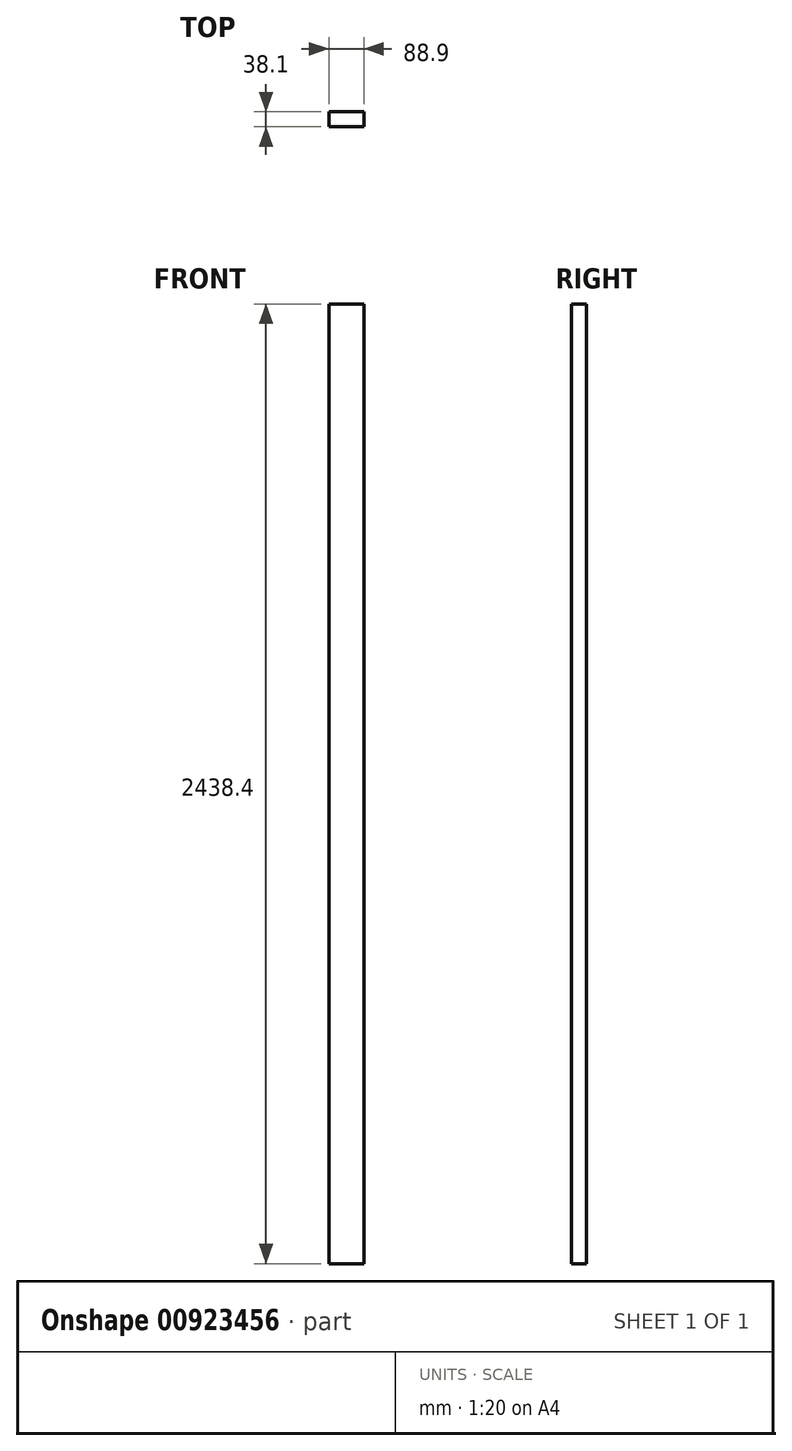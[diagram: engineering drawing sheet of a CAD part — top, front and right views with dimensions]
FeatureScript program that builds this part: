
annotation { "Feature Type Name" : "Feature", "Feature Type Description" : "" }
export const myFeature = defineFeature(function(context is Context, id is Id, definition is map)
    precondition{}
    {
        {
            var Q0;
            Q0=qCreatedBy(makeId("Top.planeOp"),FACE);
            var sketch = newSketch(context, id + "F0", { "sketchPlane" : qUnion([Q0])});
            skLineSegment(sketch, "E0.bottom", {"start": v(0, 0) * mm, "end": v(88.9, 0) * mm});
            skLineSegment(sketch, "E0.top", {"start": v(0, 38.1) * mm, "end": v(88.9, 38.1) * mm});
            skLineSegment(sketch, "E0.left", {"start": v(0, 0) * mm, "end": v(0, 38.1) * mm});
            skLineSegment(sketch, "E0.right", {"start": v(88.9, 0) * mm, "end": v(88.9, 38.1) * mm});
            skSolve(sketch);
        }
        {
            var Q0;
            Q0=makeQuery(id+"F0.imprint","IMPRINT",FACE,{"disambiguationData":[TD([[makeQuery(id+"F0.imprint","IMPRINT",EDGE,{"derivedFrom":sQuery(id+"F0.wireOp",EDGE,"E0.bottom")}),1.0]])]});
            extrude(context, id + "F1", {"entities" : qUnion([Q0]), "depth" : 2438.4 * mm, "offsetDistance" : 25.4 * mm});
        }
    });
